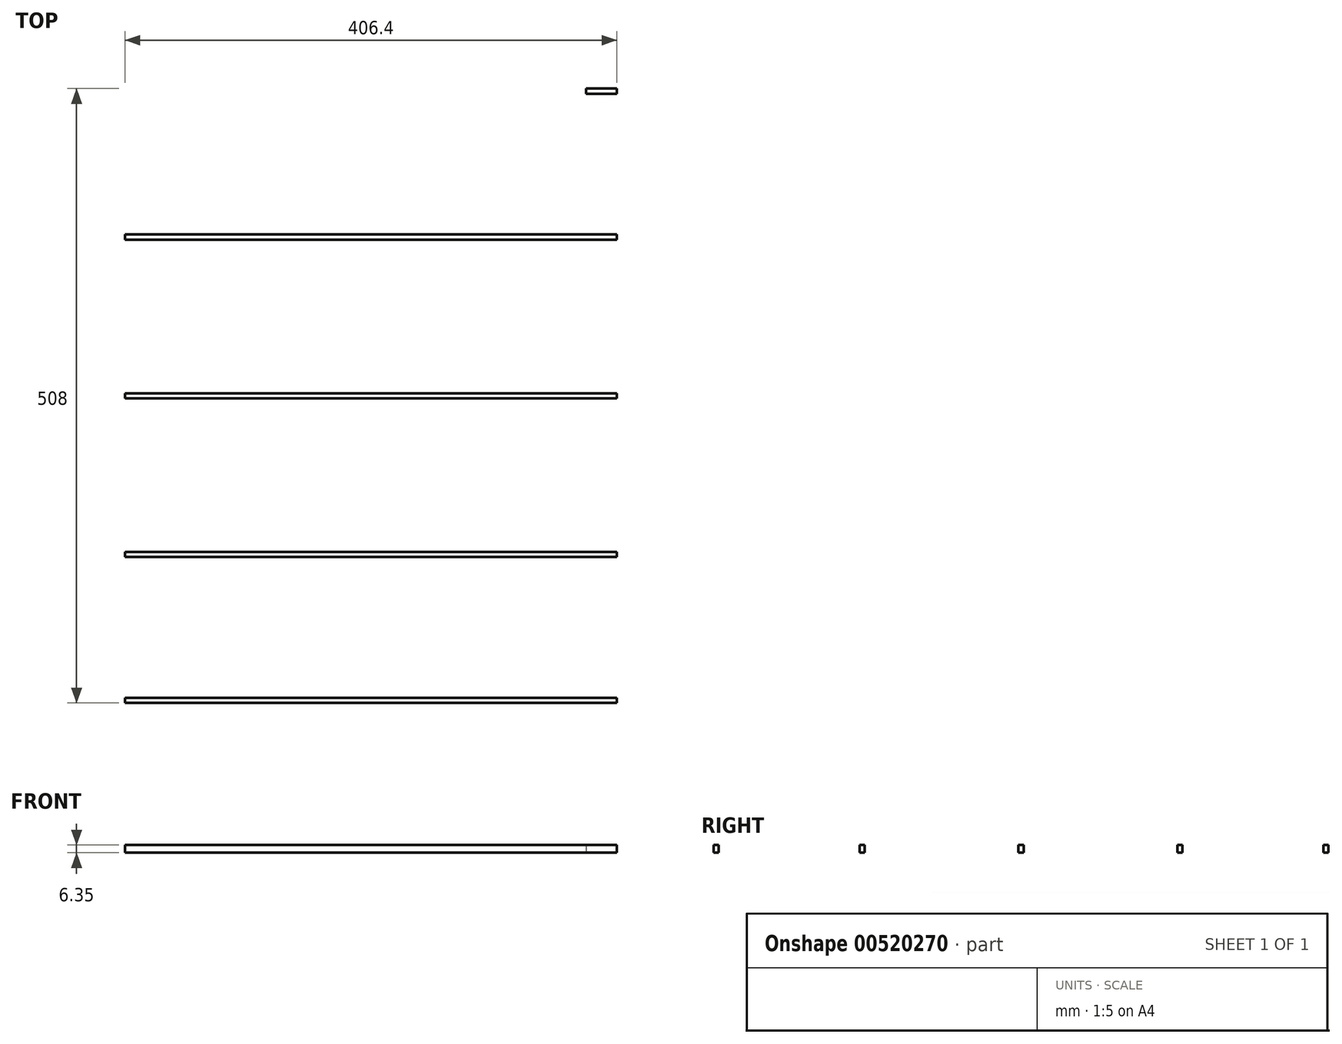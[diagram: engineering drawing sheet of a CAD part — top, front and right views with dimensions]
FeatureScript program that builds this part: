
annotation { "Feature Type Name" : "Feature", "Feature Type Description" : "" }
export const myFeature = defineFeature(function(context is Context, id is Id, definition is map)
    precondition{}
    {
        {
            var Q0;
            Q0=qCreatedBy(makeId("Top.planeOp"),FACE);
            var sketch = newSketch(context, id + "F0", { "sketchPlane" : qUnion([Q0])});
            skLineSegment(sketch, "E0.bottom", {"start": v(190.5, 254) * mm, "end": v(-190.5, 254) * mm});
            skLineSegment(sketch, "E0.top", {"start": v(190.5, -254) * mm, "end": v(-190.5, -254) * mm});
            skLineSegment(sketch, "E0.left", {"start": v(190.5, 254) * mm, "end": v(190.5, -254) * mm});
            skLineSegment(sketch, "E0.right", {"start": v(-190.5, 254) * mm, "end": v(-190.5, -254) * mm});
            skPoint(sketch, "E0.middle", {"position": v(0, 0) * mm});
            skLineSegment(sketch, "E1", {"start": v(-190.5, 0) * mm, "end": v(190.5, 0) * mm, "construction": true});
            skLineSegment(sketch, "E2.bottom", {"start": v(-190.5, 2.12) * mm, "end": v(215.9, 2.12) * mm});
            skLineSegment(sketch, "E2.top", {"start": v(-190.5, -2.12) * mm, "end": v(215.9, -2.12) * mm});
            skLineSegment(sketch, "E2.left", {"start": v(-190.5, 2.12) * mm, "end": v(-190.5, -2.12) * mm});
            skLineSegment(sketch, "E2.right", {"start": v(215.9, 2.12) * mm, "end": v(215.9, -2.12) * mm});
            skLineSegment(sketch, "E3.bottom", {"start": v(-190.5, 129.12) * mm, "end": v(215.9, 129.12) * mm});
            skLineSegment(sketch, "E3.top", {"start": v(-190.5, 133.35) * mm, "end": v(215.9, 133.35) * mm});
            skLineSegment(sketch, "E3.left", {"start": v(-190.5, 129.12) * mm, "end": v(-190.5, 133.35) * mm});
            skLineSegment(sketch, "E3.right", {"start": v(215.9, 129.12) * mm, "end": v(215.9, 133.35) * mm});
            skLineSegment(sketch, "E4.bottom", {"start": v(-190.5, 254) * mm, "end": v(215.9, 254) * mm});
            skLineSegment(sketch, "E4.top", {"start": v(-190.5, 249.77) * mm, "end": v(215.9, 249.77) * mm});
            skLineSegment(sketch, "E4.left", {"start": v(-190.5, 254) * mm, "end": v(-190.5, 249.77) * mm});
            skLineSegment(sketch, "E4.right", {"start": v(215.9, 254) * mm, "end": v(215.9, 249.77) * mm});
            skLineSegment(sketch, "E5.MirrorCS", {"start": v(-190.5, -129.12) * mm, "end": v(215.9, -129.12) * mm});
            skLineSegment(sketch, "E6.MirrorCS", {"start": v(-190.5, -129.12) * mm, "end": v(-190.5, -133.35) * mm});
            skLineSegment(sketch, "E7.MirrorCS", {"start": v(-190.5, -133.35) * mm, "end": v(215.9, -133.35) * mm});
            skLineSegment(sketch, "E8.MirrorCS", {"start": v(215.9, -129.12) * mm, "end": v(215.9, -133.35) * mm});
            skLineSegment(sketch, "E9.MirrorCS", {"start": v(-190.5, -249.77) * mm, "end": v(215.9, -249.77) * mm});
            skLineSegment(sketch, "E10.MirrorCS", {"start": v(215.9, -254) * mm, "end": v(215.9, -249.77) * mm});
            skLineSegment(sketch, "E11.MirrorCS", {"start": v(-190.5, -254) * mm, "end": v(-190.5, 254) * mm});
            skLineSegment(sketch, "E12", {"start": v(-190.5, -254) * mm, "end": v(215.9, -254) * mm});
            skSolve(sketch);
        }
        {
            var Q0;
            {var subQ0=sQuery(id+"F0.wireOp",EDGE,"E4.bottom");Q0=makeQuery(id+"F0.imprint","IMPRINT",FACE,{"disambiguationData":[TD([[makeQuery(id+"F0.imprint","IMPRINT",EDGE,{"derivedFrom":subQ0}),-1.0]])]});}
            var Q1;
            {var subQ0=sQuery(id+"F0.wireOp",EDGE,"E3.bottom");Q1=makeQuery(id+"F0.imprint","IMPRINT",FACE,{"disambiguationData":[TD([[makeQuery(id+"F0.imprint","IMPRINT",EDGE,{"derivedFrom":subQ0}),1.0]])]});}
            var Q2;
            {var subQ0=sQuery(id+"F0.wireOp",EDGE,"E2.bottom");Q2=makeQuery(id+"F0.imprint","IMPRINT",FACE,{"disambiguationData":[TD([[makeQuery(id+"F0.imprint","IMPRINT",EDGE,{"derivedFrom":subQ0}),-1.0]])]});}
            var Q3;
            {var subQ0=sQuery(id+"F0.wireOp",EDGE,"E5.MirrorCS");Q3=makeQuery(id+"F0.imprint","IMPRINT",FACE,{"disambiguationData":[TD([[makeQuery(id+"F0.imprint","IMPRINT",EDGE,{"derivedFrom":subQ0}),-1.0]])]});}
            var Q4;
            {var subQ4=sQuery(id+"F0.wireOp",EDGE,"E9.MirrorCS");Q4=makeQuery(id+"F0.imprint","IMPRINT",FACE,{"disambiguationData":[TD([[makeQuery(id+"F0.imprint","IMPRINT",EDGE,{"derivedFrom":subQ4}),-1.0]])]});}
            extrude(context, id + "F1", {"entities" : qUnion([Q0, Q1, Q2, Q3, Q4]), "depth" : 6.35 * mm, "offsetDistance" : 25.4 * mm});
        }
    });
